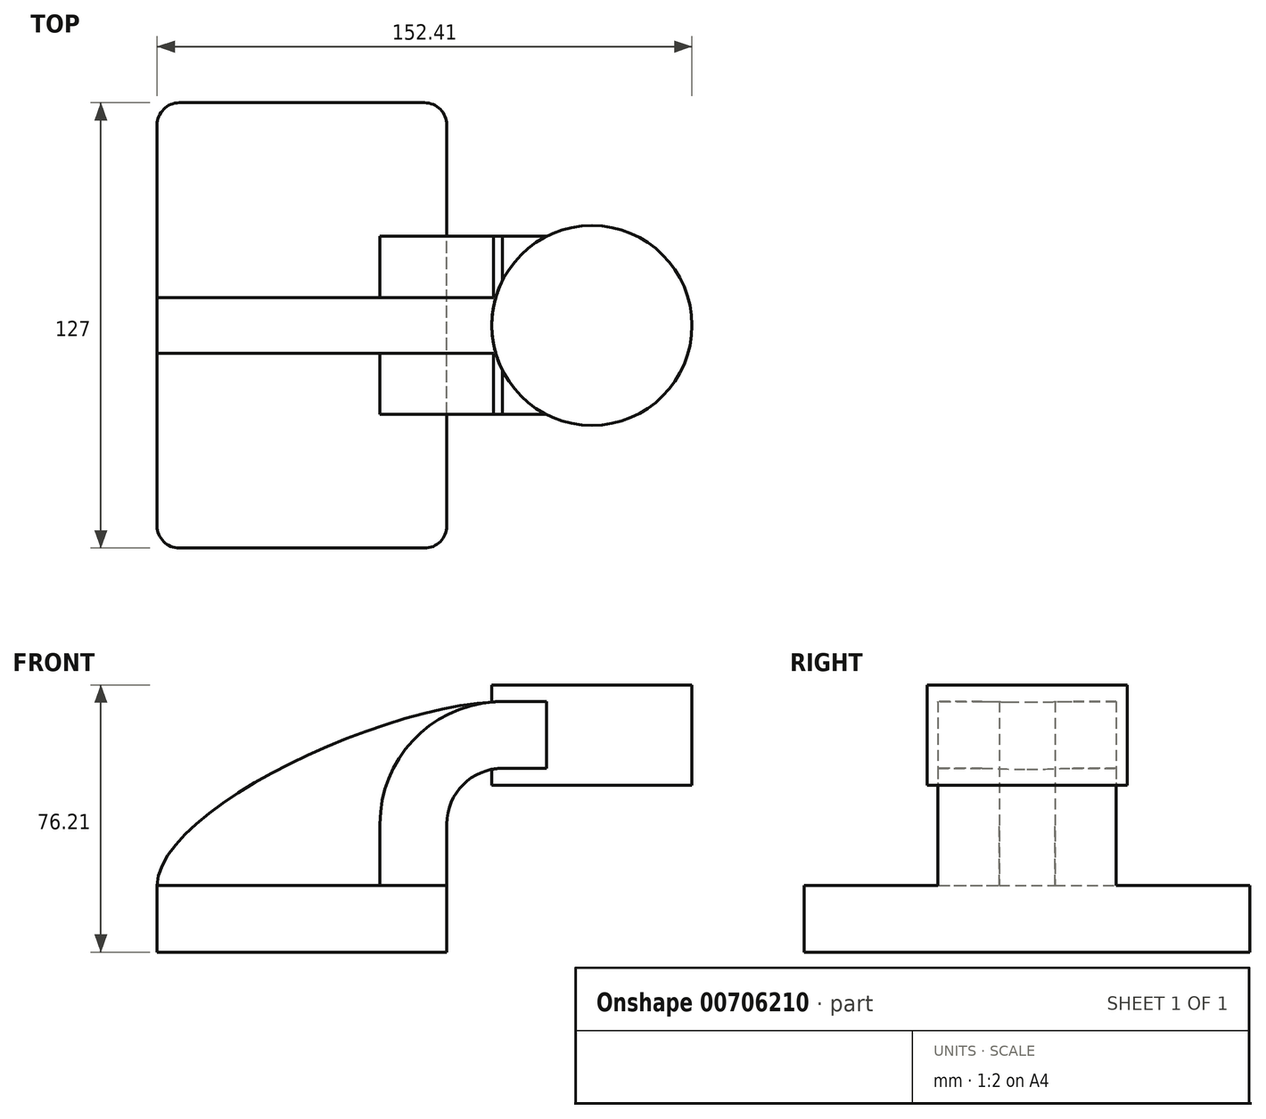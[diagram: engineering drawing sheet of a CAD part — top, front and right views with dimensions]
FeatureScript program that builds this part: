
annotation { "Feature Type Name" : "Feature", "Feature Type Description" : "" }
export const myFeature = defineFeature(function(context is Context, id is Id, definition is map)
    precondition{}
    {
        {
            var Q0;
            Q0=qCreatedBy(makeId("Front.planeOp"),FACE);
            var sketch = newSketch(context, id + "F0", { "sketchPlane" : qUnion([Q0])});
            skLineSegment(sketch, "E0.bottom", {"start": v(41.27, 9.53) * mm, "end": v(-41.28, 9.53) * mm});
            skLineSegment(sketch, "E0.top", {"start": v(41.28, -9.52) * mm, "end": v(-41.27, -9.52) * mm});
            skLineSegment(sketch, "E0.left", {"start": v(41.28, 9.53) * mm, "end": v(41.28, -9.52) * mm});
            skLineSegment(sketch, "E0.right", {"start": v(-41.28, 9.53) * mm, "end": v(-41.27, -9.52) * mm});
            skPoint(sketch, "E0.middle", {"position": v(0, 0) * mm});
            skLineSegment(sketch, "E1.bottom", {"start": v(111.12, 38.1) * mm, "end": v(60.32, 38.1) * mm});
            skLineSegment(sketch, "E1.top", {"start": v(111.12, 66.68) * mm, "end": v(60.32, 66.68) * mm});
            skLineSegment(sketch, "E1.left", {"start": v(111.12, 38.1) * mm, "end": v(111.12, 66.68) * mm});
            skLineSegment(sketch, "E1.right", {"start": v(60.32, 38.1) * mm, "end": v(60.32, 66.68) * mm});
            skPoint(sketch, "E1.middle", {"position": v(85.72, 52.39) * mm});
            skLineSegment(sketch, "E2", {"start": v(41.27, 9.53) * mm, "end": v(41.27, 27) * mm});
            skArc(sketch, "E3", {"start": v(41.27, 27) * mm, "mid": v(45.92, 38.23) * mm, "end": v(57.15, 42.88) * mm});
            skLineSegment(sketch, "E4", {"start": v(57.15, 42.88) * mm, "end": v(82.61, 42.88) * mm});
            skLineSegment(sketch, "E5.0", {"start": v(57.15, 61.93) * mm, "end": v(82.61, 61.93) * mm});
            skArc(sketch, "E5.1", {"start": v(22.23, 27) * mm, "mid": v(32.45, 51.7) * mm, "end": v(57.15, 61.93) * mm});
            skLineSegment(sketch, "E5.2", {"start": v(22.23, 9.53) * mm, "end": v(22.23, 27) * mm});
            skLineSegment(sketch, "E6", {"start": v(82.61, 38.1) * mm, "end": v(82.61, 66.68) * mm});
            skFitSpline(sketch, "E7", {"points": [v(57.15, 61.93) * mm, v(-41.28, 9.53) * mm], "startDerivative": vector(-101.5, -1.62) * mm, "endDerivative": vector(-1.29, -64.76) * mm});
            skSolve(sketch);
        }
        {
            var Q0;
            Q0=makeQuery(id+"F0.imprint","IMPRINT",FACE,{"disambiguationData":[TD([[makeQuery(id+"F0.imprint","IMPRINT",EDGE,{"derivedFrom":sQuery(id+"F0.wireOp",EDGE,"E0.top")}),-1.0]])]});
            extrude(context, id + "F1", {"entities" : qUnion([Q0]), "endBound" : BoundingType.SYMMETRIC, "depth" : 127 * mm, "offsetDistance" : 25.4 * mm});
        }
        {
            var Q0;
            {var subQ0=sQuery(id+"F0.wireOp",EDGE,"E4");var subQ1=sQuery(id+"F0.wireOp",EDGE,"E1.right");var subQ2=makeQuery(id+"F0.imprint","INTERSECT",VERTEX,{"derivedFrom":[subQ1,subQ0]});Q0=makeQuery(id+"F0.imprint","IMPRINT",FACE,{"disambiguationData":[TD([[makeQuery(id+"F0.imprint","IMPRINT",EDGE,{"disambiguationData":[TD([[subQ2,-1.0]])],"derivedFrom":subQ1}),-1.0]])]});}
            var Q1;
            {var subQ6=sQuery(id+"F0.wireOp",EDGE,"E2");Q1=makeQuery(id+"F0.imprint","IMPRINT",FACE,{"disambiguationData":[TD([[makeQuery(id+"F0.imprint","IMPRINT",EDGE,{"derivedFrom":subQ6}),1.0]])]});}
            extrude(context, id + "F2", {"entities" : qUnion([Q0, Q1]), "operationType" : NewBodyOperationType.ADD, "endBound" : BoundingType.SYMMETRIC, "depth" : 50.8 * mm, "offsetDistance" : 25.4 * mm});
        }
        {
            var Q0;
            {var subQ3=sQuery(id+"F0.wireOp",EDGE,"E5.2");Q0=makeQuery(id+"F0.imprint","IMPRINT",FACE,{"disambiguationData":[TD([[makeQuery(id+"F0.imprint","IMPRINT",EDGE,{"derivedFrom":subQ3}),1.0]])]});}
            extrude(context, id + "F3", {"entities" : qUnion([Q0]), "operationType" : NewBodyOperationType.ADD, "endBound" : BoundingType.SYMMETRIC, "depth" : 15.88 * mm, "offsetDistance" : 25.4 * mm});
        }
        {
            var Q0;
            {var subQ0=sQuery(id+"F0.wireOp",EDGE,"E1.left");Q0=makeQuery(id+"F0.imprint","IMPRINT",FACE,{"disambiguationData":[TD([[makeQuery(id+"F0.imprint","IMPRINT",EDGE,{"derivedFrom":subQ0}),1.0]])]});}
            var Q1;
            Q1=sQuery(id+"F0.wireOp",EDGE,"E6");
            revolve(context, id + "F4", {"operationType" : NewBodyOperationType.ADD, "entities" : qUnion([Q0]), "axis" : qUnion([Q1]), "revolveType" : RevolveType.FULL});
        }
        {
            var Q0;
            Q0=makeQuery(id+"F1.opExtrude","CAP_EDGE",EDGE,{"disambiguationData":[OSD([sQuery(id+"F0.wireOp",EDGE,"E0.left")])],"isStart":false});
            var Q1;
            Q1=makeQuery(id+"F1.opExtrude","CAP_EDGE",EDGE,{"disambiguationData":[OSD([sQuery(id+"F0.wireOp",EDGE,"E0.right")])],"isStart":false});
            var Q2;
            Q2=makeQuery(id+"F1.opExtrude","CAP_EDGE",EDGE,{"disambiguationData":[OSD([sQuery(id+"F0.wireOp",EDGE,"E0.left")])],"isStart":true});
            var Q3;
            Q3=makeQuery(id+"F1.opExtrude","CAP_EDGE",EDGE,{"disambiguationData":[OSD([sQuery(id+"F0.wireOp",EDGE,"E0.right")])],"isStart":true});
            fillet(context, id + "F5", {"entities" : qUnion([Q0, Q1, Q2, Q3]), "radius" : 6.35 * mm, "tangentPropagation" : true, "allowEdgeOverflow" : false});
        }
    });
